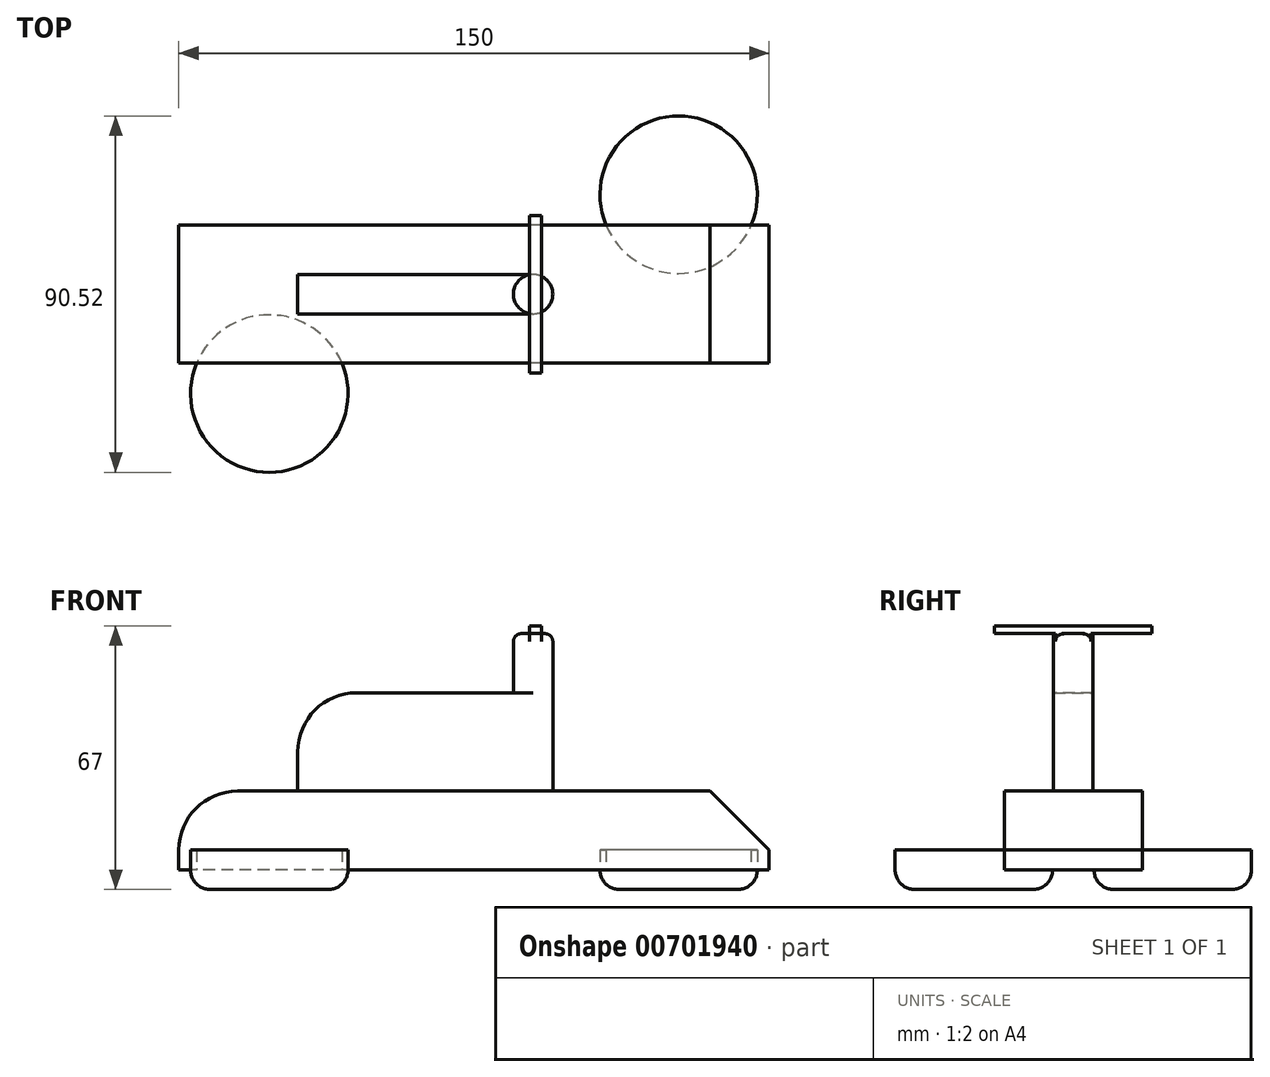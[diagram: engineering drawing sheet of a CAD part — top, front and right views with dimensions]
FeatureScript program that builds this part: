
annotation { "Feature Type Name" : "Feature", "Feature Type Description" : "" }
export const myFeature = defineFeature(function(context is Context, id is Id, definition is map)
    precondition{}
    {
        {
            var Q0;
            Q0=qCreatedBy(makeId("Top.planeOp"),FACE);
            var sketch = newSketch(context, id + "F0", { "sketchPlane" : qUnion([Q0])});
            skLineSegment(sketch, "E0.bottom", {"start": v(75, -17.5) * mm, "end": v(-75, -17.5) * mm});
            skLineSegment(sketch, "E0.top", {"start": v(75, 17.5) * mm, "end": v(-75, 17.5) * mm});
            skLineSegment(sketch, "E0.left", {"start": v(75, -17.5) * mm, "end": v(75, 17.5) * mm});
            skLineSegment(sketch, "E0.right", {"start": v(-75, -17.5) * mm, "end": v(-75, 17.5) * mm});
            skPoint(sketch, "E0.middle", {"position": v(0, 0) * mm});
            skSolve(sketch);
        }
        {
            var Q0;
            Q0=makeQuery(id+"F0.imprint","IMPRINT",FACE,{"disambiguationData":[TD([[makeQuery(id+"F0.imprint","IMPRINT",EDGE,{"derivedFrom":sQuery(id+"F0.wireOp",EDGE,"E0.bottom")}),-1.0]])]});
            extrude(context, id + "F1", {"entities" : qUnion([Q0]), "endBound" : BoundingType.SYMMETRIC, "depth" : 20 * mm, "offsetDistance" : 25 * mm});
        }
        {
            var Q0;
            Q0=qCreatedBy(makeId("Top.planeOp"),FACE);
            cPlane(context, id + "F2", {"entities" : qUnion([Q0]), "cplaneType" : CPlaneType.OFFSET, "offset" : 10 * mm, "oppositeDirection" : true, "width" : 150 * mm, "height" : 150 * mm});
        }
        {
            var Q0;
            Q0=qCreatedBy(id+"F2.planeOp",FACE);
            var sketch = newSketch(context, id + "F3", { "sketchPlane" : qUnion([Q0])});
            skCircle(sketch, "E1", {"center": v(-52, -25.26) * mm, "radius": 20 * mm});
            skCircle(sketch, "E2.MirrorC", {"center": v(-52, 25.26) * mm, "radius": 20 * mm});
            skCircle(sketch, "E3.MirrorC", {"center": v(52, 25.26) * mm, "radius": 20 * mm});
            skCircle(sketch, "E4.MirrorC", {"center": v(52, -25.26) * mm, "radius": 20 * mm});
            skSolve(sketch);
        }
        {
            var Q0;
            Q0=makeQuery(id+"F3.imprint","IMPRINT",FACE,{"disambiguationData":[TD([[makeQuery(id+"F3.imprint","IMPRINT",EDGE,{"derivedFrom":sQuery(id+"F3.wireOp",EDGE,"E1")}),1.0]])]});
            var Q1;
            Q1=makeQuery(id+"F3.imprint","IMPRINT",FACE,{"disambiguationData":[TD([[makeQuery(id+"F3.imprint","IMPRINT",EDGE,{"derivedFrom":sQuery(id+"F3.wireOp",EDGE,"E4.MirrorC")}),-1.0]])]});
            var Q2;
            Q2=makeQuery(id+"F3.imprint","IMPRINT",FACE,{"disambiguationData":[TD([[makeQuery(id+"F3.imprint","IMPRINT",EDGE,{"derivedFrom":sQuery(id+"F3.wireOp",EDGE,"E3.MirrorC")}),1.0]])]});
            var Q3;
            Q3=makeQuery(id+"F3.imprint","IMPRINT",FACE,{"disambiguationData":[TD([[makeQuery(id+"F3.imprint","IMPRINT",EDGE,{"derivedFrom":sQuery(id+"F3.wireOp",EDGE,"E2.MirrorC")}),-1.0]])]});
            extrude(context, id + "F4", {"entities" : qUnion([Q0, Q1, Q2, Q3]), "operationType" : NewBodyOperationType.ADD, "endBound" : BoundingType.SYMMETRIC, "depth" : 10 * mm, "offsetDistance" : 25 * mm});
        }
        {
            var Q0;
            Q0=makeQuery(id+"F1.opExtrude","CAP_EDGE",EDGE,{"disambiguationData":[OSD([sQuery(id+"F0.wireOp",EDGE,"E0.right")])],"isStart":false});
            fillet(context, id + "F5", {"entities" : qUnion([Q0]), "radius" : 15 * mm, "tangentPropagation" : true, "allowEdgeOverflow" : false});
        }
        {
            var Q0;
            Q0=makeQuery(id+"F1.opExtrude","CAP_EDGE",EDGE,{"disambiguationData":[OSD([sQuery(id+"F0.wireOp",EDGE,"E0.left")])],"isStart":false});
            chamfer(context, id + "F6", {"entities" : qUnion([Q0]), "width" : 15 * mm, "tangentPropagation" : true});
        }
        {
            var Q0;
            Q0=makeQuery(id+"F4.opExtrude","CAP_EDGE",EDGE,{"disambiguationData":[OSD([sQuery(id+"F3.wireOp",EDGE,"E4.MirrorC")])],"isStart":true});
            var Q1;
            Q1=makeQuery(id+"F4.opExtrude","CAP_EDGE",EDGE,{"disambiguationData":[OSD([sQuery(id+"F3.wireOp",EDGE,"E3.MirrorC")])],"isStart":true});
            var Q2;
            Q2=makeQuery(id+"F4.opExtrude","CAP_EDGE",EDGE,{"disambiguationData":[OSD([sQuery(id+"F3.wireOp",EDGE,"E1")])],"isStart":true});
            var Q3;
            Q3=makeQuery(id+"F4.opExtrude","CAP_EDGE",EDGE,{"disambiguationData":[OSD([sQuery(id+"F3.wireOp",EDGE,"E2.MirrorC")])],"isStart":true});
            fillet(context, id + "F7", {"entities" : qUnion([Q0, Q1, Q2, Q3]), "radius" : 5 * mm, "tangentPropagation" : true, "allowEdgeOverflow" : false});
        }
        {
            var Q0;
            Q0=makeQuery(id+"F1.opExtrude","CAP_FACE",FACE,{"disambiguationData":[OSD([sQuery(id+"F0.wireOp",EDGE,"E0.bottom"),sQuery(id+"F0.wireOp",EDGE,"E0.top"),sQuery(id+"F0.wireOp",EDGE,"E0.left"),sQuery(id+"F0.wireOp",EDGE,"E0.right")])],"isStart":false});
            cPlane(context, id + "F8", {"entities" : qUnion([Q0]), "cplaneType" : CPlaneType.OFFSET, "offset" : 0 * mm, "width" : 150 * mm, "height" : 150 * mm});
        }
        {
            var Q0;
            Q0=qCreatedBy(id+"F8.planeOp",FACE);
            var sketch = newSketch(context, id + "F9", { "sketchPlane" : qUnion([Q0])});
            skLineSegment(sketch, "E5.bottom", {"start": v(25.24, -5) * mm, "end": v(-44.76, -5) * mm});
            skLineSegment(sketch, "E5.top", {"start": v(25.24, 5) * mm, "end": v(-44.76, 5) * mm});
            skLineSegment(sketch, "E5.left", {"start": v(25.24, -5) * mm, "end": v(25.24, 5) * mm});
            skLineSegment(sketch, "E5.right", {"start": v(-44.76, -5) * mm, "end": v(-44.76, 5) * mm});
            skPoint(sketch, "E5.middle", {"position": v(-9.76, 0) * mm});
            skCircle(sketch, "E6", {"center": v(15.02, 0) * mm, "radius": 5 * mm});
            skPoint(sketch, "E6.centerSnap0", {"position": v(25.24, 0) * mm});
            skSolve(sketch);
        }
        {
            var Q0;
            {var subQ0=sQuery(id+"F9.wireOp",EDGE,"E6");var subQ1=makeQuery(id+"F9.imprint","INTERSECT",VERTEX,{"derivedFrom":[sQuery(id+"F9.wireOp",EDGE,"E5.bottom"),subQ0]});Q0=makeQuery(id+"F9.imprint","IMPRINT",FACE,{"disambiguationData":[TD([[makeQuery(id+"F9.imprint","IMPRINT",EDGE,{"disambiguationData":[TD([[subQ1,1.0]])],"derivedFrom":subQ0}),1.0]])]});}
            extrude(context, id + "F10", {"entities" : qUnion([Q0]), "operationType" : NewBodyOperationType.ADD, "depth" : 40 * mm, "offsetDistance" : 25 * mm});
        }
        {
            var Q0;
            {var subQ0=sQuery(id+"F9.wireOp",EDGE,"E5.right");Q0=makeQuery(id+"F9.imprint","IMPRINT",FACE,{"disambiguationData":[TD([[makeQuery(id+"F9.imprint","IMPRINT",EDGE,{"derivedFrom":subQ0}),-1.0]])]});}
            extrude(context, id + "F11", {"entities" : qUnion([Q0]), "operationType" : NewBodyOperationType.ADD, "depth" : 25 * mm, "offsetDistance" : 25 * mm});
        }
        {
            var Q0;
            Q0=makeQuery(id+"F11.opExtrude","CAP_EDGE",EDGE,{"disambiguationData":[OSD([sQuery(id+"F9.wireOp",EDGE,"E5.right")])],"isStart":false});
            fillet(context, id + "F12", {"entities" : qUnion([Q0]), "radius" : 15 * mm, "tangentPropagation" : true, "allowEdgeOverflow" : false});
        }
        {
            var Q0;
            Q0=makeQuery(id+"F10.opExtrude","CAP_FACE",FACE,{"disambiguationData":[OSD([sQuery(id+"F9.wireOp",EDGE,"E6")])],"isStart":false});
            cPlane(context, id + "F13", {"entities" : qUnion([Q0]), "cplaneType" : CPlaneType.OFFSET, "offset" : 0 * mm, "width" : 150 * mm, "height" : 150 * mm});
        }
        {
            var Q0;
            Q0=qCreatedBy(id+"F13.planeOp",FACE);
            var sketch = newSketch(context, id + "F14", { "sketchPlane" : qUnion([Q0])});
            skLineSegment(sketch, "E7.bottom", {"start": v(14.12, -20) * mm, "end": v(17.12, -20) * mm});
            skLineSegment(sketch, "E7.top", {"start": v(14.12, 20) * mm, "end": v(17.12, 20) * mm});
            skLineSegment(sketch, "E7.left", {"start": v(14.12, -20) * mm, "end": v(14.12, 20) * mm});
            skLineSegment(sketch, "E7.right", {"start": v(17.12, -20) * mm, "end": v(17.12, 20) * mm});
            skPoint(sketch, "E7.middle", {"position": v(15.62, 0) * mm});
            skSolve(sketch);
        }
        {
            var Q0;
            Q0=makeQuery(id+"F14.imprint","IMPRINT",FACE,{"disambiguationData":[TD([[makeQuery(id+"F14.imprint","IMPRINT",EDGE,{"derivedFrom":sQuery(id+"F14.wireOp",EDGE,"E7.bottom")}),1.0]])]});
            extrude(context, id + "F15", {"entities" : qUnion([Q0]), "operationType" : NewBodyOperationType.ADD, "depth" : 2 * mm, "offsetDistance" : 25 * mm});
        }
        {
            var Q0;
            {var subQ0=sQuery(id+"F9.wireOp",EDGE,"E6");var subQ1=makeQuery(id+"F10.opExtrude","SWEPT_FACE",FACE,{"disambiguationData":[OSD([subQ0])]});var subQ2=makeQuery(id+"F10.opExtrude","CAP_FACE",FACE,{"disambiguationData":[OSD([subQ0])],"isStart":false});var subQ3=sQuery(id+"F14.wireOp",EDGE,"E7.right");Q0=makeQuery(id+"F15.boolean.opBoolean","SPLIT",EDGE,{"disambiguationData":[topologyDisambiguationEdgeConnected([subQ1,subQ2]),TD([makeQuery(id+"F15.opExtrude","SWEPT_FACE",FACE,{"disambiguationData":[OSD([subQ3])]})])],"derivedFrom":makeQuery(id+"F10.opExtrude","CAP_EDGE",EDGE,{"disambiguationData":[OSD([subQ0])],"isStart":false})});}
            var Q1;
            {var subQ0=sQuery(id+"F9.wireOp",EDGE,"E6");var subQ1=makeQuery(id+"F10.opExtrude","SWEPT_FACE",FACE,{"disambiguationData":[OSD([subQ0])]});var subQ2=makeQuery(id+"F10.opExtrude","CAP_FACE",FACE,{"disambiguationData":[OSD([subQ0])],"isStart":false});var subQ3=sQuery(id+"F14.wireOp",EDGE,"E7.left");Q1=makeQuery(id+"F15.boolean.opBoolean","SPLIT",EDGE,{"disambiguationData":[topologyDisambiguationEdgeConnected([subQ1,subQ2]),TD([makeQuery(id+"F15.opExtrude","SWEPT_FACE",FACE,{"disambiguationData":[OSD([subQ3])]})])],"derivedFrom":makeQuery(id+"F10.opExtrude","CAP_EDGE",EDGE,{"disambiguationData":[OSD([subQ0])],"isStart":false})});}
            fillet(context, id + "F16", {"entities" : qUnion([Q0, Q1]), "radius" : 2 * mm, "tangentPropagation" : true, "allowEdgeOverflow" : false});
        }
    });
